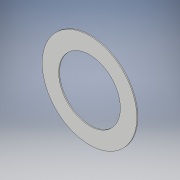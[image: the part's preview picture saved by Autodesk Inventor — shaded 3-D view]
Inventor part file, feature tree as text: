
AUTODESK INVENTOR PART (.ipt)
format: ipt  version: 2019 (Build 230136000, 136)  size: 216,064 bytes
history: native  units: mm
features: other x4, reference x2, extrude x1, sketch x1
ambient origin geometry x8: Origin, YZ Plane, XZ Plane, XY Plane, X Axis, Y Axis, Z Axis, Center Point
bodies: Body1 (feature_tree)
feature tree (8):
  extrude  "Выдавливание2"  Depth=1.5mm TaperAngle=0.0deg
  sketch  "Эскиз3"
  reference  "Ссылка5"
  reference  "Ссылка6"
  other  "<userpath>\Documents\GitHub\Tesla_coil_V1\3dModels\TeslaCoil.iam"
  other  "TeslaCoil.iam"
  other  "Cap:2"
  other  "RackeSecondary:1"
